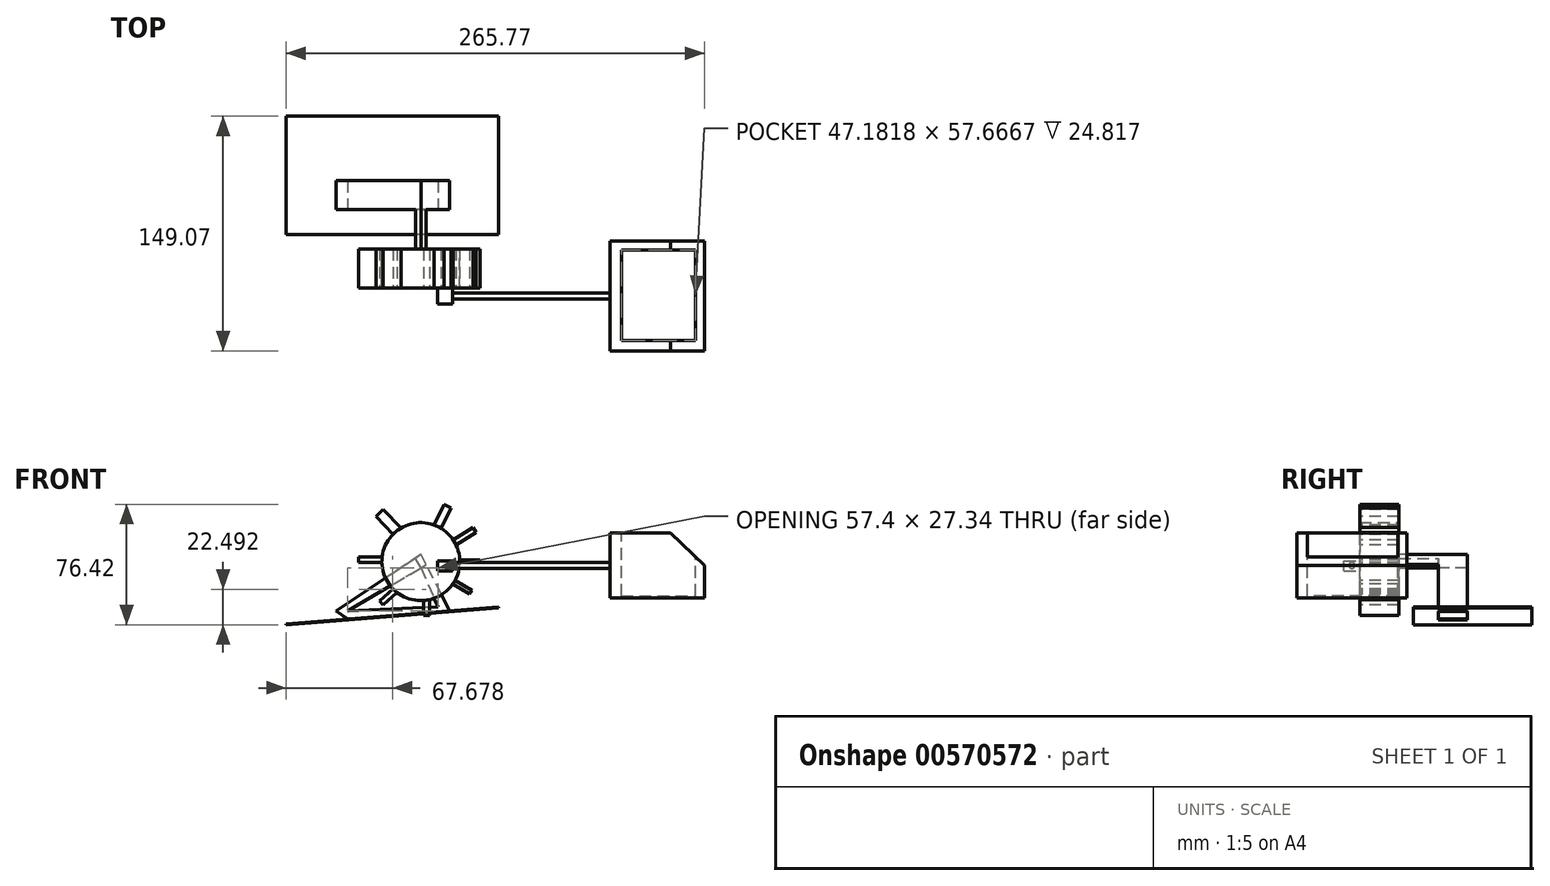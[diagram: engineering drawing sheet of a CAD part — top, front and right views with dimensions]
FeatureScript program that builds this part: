
annotation { "Feature Type Name" : "Feature", "Feature Type Description" : "" }
export const myFeature = defineFeature(function(context is Context, id is Id, definition is map)
    precondition{}
    {
        {
            var Q0;
            Q0=qCreatedBy(makeId("Top.planeOp"),FACE);
            var sketch = newSketch(context, id + "F0", { "sketchPlane" : qUnion([Q0])});
            skLineSegment(sketch, "E0.bottom", {"start": v(40, 9.15) * mm, "end": v(-40, 9.15) * mm});
            skLineSegment(sketch, "E0.top", {"start": v(40, -9.15) * mm, "end": v(-40, -9.15) * mm});
            skLineSegment(sketch, "E0.left", {"start": v(40, 9.15) * mm, "end": v(40, -9.15) * mm});
            skLineSegment(sketch, "E0.right", {"start": v(-40, 9.15) * mm, "end": v(-40, -9.15) * mm});
            skPoint(sketch, "E0.middle", {"position": v(0, 0) * mm});
            skSolve(sketch);
        }
        {
            var Q0;
            Q0=makeQuery(id+"F0.imprint","IMPRINT",FACE,{"disambiguationData":[TD([[makeQuery(id+"F0.imprint","IMPRINT",EDGE,{"derivedFrom":sQuery(id+"F0.wireOp",EDGE,"E0.bottom")}),1.0]])]});
            extrude(context, id + "F1", {"entities" : qUnion([Q0]), "depth" : 50 * mm, "offsetDistance" : 25 * mm});
        }
        {
            var Q0;
            Q0=makeQuery(id+"F1.opExtrude","SWEPT_FACE",FACE,{"disambiguationData":[OSD([sQuery(id+"F0.wireOp",EDGE,"E0.top")])]});
            var sketch = newSketch(context, id + "F2", { "sketchPlane" : qUnion([Q0])});
            skLineSegment(sketch, "E1", {"start": v(-29.15, 11.41) * mm, "end": v(17.63, 38.75) * mm});
            skLineSegment(sketch, "E2", {"start": v(17.63, 38.75) * mm, "end": v(28.25, 13.9) * mm});
            skLineSegment(sketch, "E3", {"start": v(28.25, 13.9) * mm, "end": v(-29.15, 11.41) * mm});
            skLineSegment(sketch, "E4", {"start": v(-29.15, 6.21) * mm, "end": v(35.7, 11.41) * mm});
            skLineSegment(sketch, "E5", {"start": v(35.7, 11.41) * mm, "end": v(17.63, 47.11) * mm});
            skLineSegment(sketch, "E6", {"start": v(17.63, 47.11) * mm, "end": v(-36.38, 11.41) * mm});
            skLineSegment(sketch, "E7", {"start": v(-36.38, 11.41) * mm, "end": v(-29.15, 6.21) * mm});
            skSolve(sketch);
        }
        {
            var Q0;
            Q0=makeQuery(id+"F2.imprint","IMPRINT",FACE,{"disambiguationData":[TD([[makeQuery(id+"F2.imprint","IMPRINT",EDGE,{"derivedFrom":sQuery(id+"F2.wireOp",EDGE,"E4")}),-1.0]])]});
            var Q1;
            Q1=makeQuery(id+"F2.imprint","IMPRINT",FACE,{"disambiguationData":[TD([[makeQuery(id+"F2.imprint","IMPRINT",EDGE,{"derivedFrom":sQuery(id+"F2.wireOp",EDGE,"E1")}),-1.0]])]});
            extrude(context, id + "F3", {"entities" : qUnion([Q0, Q1]), "operationType" : NewBodyOperationType.REMOVE, "endBound" : BoundingType.THROUGH_ALL, "oppositeDirection" : true, "depth" : 25 * mm, "offsetDistance" : 25 * mm});
        }
        {
            var Q0;
            Q0=makeQuery(id+"F1.opExtrude","SWEPT_FACE",FACE,{"disambiguationData":[OSD([sQuery(id+"F0.wireOp",EDGE,"E0.top")])]});
            var sketch = newSketch(context, id + "F4", { "sketchPlane" : qUnion([Q0])});
            skLineSegment(sketch, "E8", {"start": v(17.63, 38.75) * mm, "end": v(14.1, 44.78) * mm});
            skLineSegment(sketch, "E9", {"start": v(17.63, 38.75) * mm, "end": v(20.8, 40.85) * mm});
            skSolve(sketch);
        }
        {
            var Q0;
            {var subQ0=sQuery(id+"F4.wireOp",EDGE,"E8");Q0=makeQuery(id+"F4.imprint","IMPRINT",FACE,{"disambiguationData":[TD([[makeQuery(id+"F4.imprint","IMPRINT",EDGE,{"derivedFrom":subQ0}),-1.0]])]});}
            extrude(context, id + "F5", {"entities" : qUnion([Q0]), "operationType" : NewBodyOperationType.ADD, "depth" : 25 * mm, "offsetDistance" : 25 * mm});
        }
        {
            var Q0;
            Q0=makeQuery(id+"F3.boolean.opBoolean","COPY",FACE,{"derivedFrom":makeQuery(id+"F3.opExtrude","SWEPT_FACE",FACE,{"disambiguationData":[OSD([sQuery(id+"F2.wireOp",EDGE,"E4")])]})});
            var sketch = newSketch(context, id + "F6", { "sketchPlane" : qUnion([Q0])});
            skLineSegment(sketch, "E10.bottom", {"start": v(67.66, 50.07) * mm, "end": v(-67.66, 50.07) * mm});
            skLineSegment(sketch, "E10.top", {"start": v(67.66, -50.07) * mm, "end": v(-67.66, -50.07) * mm});
            skLineSegment(sketch, "E10.left", {"start": v(67.66, 50.07) * mm, "end": v(67.66, -50.07) * mm});
            skLineSegment(sketch, "E10.right", {"start": v(-67.66, 50.07) * mm, "end": v(-67.66, -50.07) * mm});
            skPoint(sketch, "E10.middle", {"position": v(0, 0) * mm});
            skSolve(sketch);
        }
        {
            var Q0;
            Q0=makeQuery(id+"F6.imprint","IMPRINT",FACE,{"disambiguationData":[TD([[makeQuery(id+"F6.imprint","IMPRINT",EDGE,{"derivedFrom":sQuery(id+"F6.wireOp",EDGE,"E10.bottom")}),1.0]])]});
            extrude(context, id + "F7", {"entities" : qUnion([Q0]), "depth" : 0.5 * mm, "offsetDistance" : 25 * mm});
        }
        {
            var Q0;
            Q0=makeQuery(id+"F5.opExtrude","CAP_FACE",FACE,{"disambiguationData":[OSD([sQuery(id+"F2.wireOp",EDGE,"E5"),sQuery(id+"F2.wireOp",EDGE,"E6"),sQuery(id+"F4.wireOp",EDGE,"E8"),sQuery(id+"F4.wireOp",EDGE,"E9")])],"isStart":false});
            var sketch = newSketch(context, id + "F8", { "sketchPlane" : qUnion([Q0])});
            skCircle(sketch, "E11", {"center": v(17.42, 42.65) * mm, "radius": 24.74 * mm});
            skLineSegment(sketch, "E12", {"start": v(42.17, 42.65) * mm, "end": v(-7.32, 42.65) * mm});
            skSolve(sketch);
        }
        {
            var Q0;
            {var subQ5=makeQuery(id+"F5.opExtrude","CAP_EDGE",EDGE,{"disambiguationData":[OSD([sQuery(id+"F4.wireOp",EDGE,"E9")])],"isStart":false});Q0=makeQuery(id+"F8.imprint","IMPRINT",FACE,{"disambiguationData":[TD([[makeQuery(id+"F8.imprint","IMPRINT",EDGE,{"derivedFrom":subQ5}),1.0]])]});}
            var Q1;
            {var subQ5=makeQuery(id+"F5.opExtrude","CAP_EDGE",EDGE,{"disambiguationData":[OSD([sQuery(id+"F2.wireOp",EDGE,"E6")])],"isStart":false});Q1=makeQuery(id+"F8.imprint","IMPRINT",FACE,{"disambiguationData":[TD([[makeQuery(id+"F8.imprint","IMPRINT",EDGE,{"derivedFrom":subQ5}),1.0]])]});}
            var Q2;
            {var subQ0=makeQuery(id+"F5.opExtrude","CAP_EDGE",EDGE,{"disambiguationData":[OSD([sQuery(id+"F2.wireOp",EDGE,"E6")])],"isStart":false});Q2=makeQuery(id+"F8.imprint","IMPRINT",FACE,{"disambiguationData":[TD([[makeQuery(id+"F8.imprint","IMPRINT",EDGE,{"derivedFrom":subQ0}),-1.0]])]});}
            var Q3;
            {var subQ0=makeQuery(id+"F5.opExtrude","CAP_EDGE",EDGE,{"disambiguationData":[OSD([sQuery(id+"F4.wireOp",EDGE,"E9")])],"isStart":false});Q3=makeQuery(id+"F8.imprint","IMPRINT",FACE,{"disambiguationData":[TD([[makeQuery(id+"F8.imprint","IMPRINT",EDGE,{"derivedFrom":subQ0}),-1.0]])]});}
            extrude(context, id + "F9", {"entities" : qUnion([Q0, Q1, Q2, Q3]), "operationType" : NewBodyOperationType.ADD, "depth" : 25 * mm, "offsetDistance" : 25 * mm});
        }
        {
            var Q0;
            Q0=makeQuery(id+"F9.opExtrude","CAP_FACE",FACE,{"disambiguationData":[OSD([sQuery(id+"F8.wireOp",EDGE,"E11")])],"isStart":false});
            var sketch = newSketch(context, id + "F10", { "sketchPlane" : qUnion([Q0])});
            skSolve(sketch);
        }
        {
            var Q0;
            Q0=makeQuery(id+"F7.opExtrude","SWEPT_FACE",FACE,{"disambiguationData":[OSD([sQuery(id+"F6.wireOp",EDGE,"E10.bottom")])]});
            extrude(context, id + "F11", {"entities" : qUnion([Q0]), "operationType" : NewBodyOperationType.REMOVE, "oppositeDirection" : true, "depth" : 25 * mm, "offsetDistance" : 25 * mm});
        }
        {
            var Q0;
            Q0=makeQuery(id+"F10.imprint","IMPRINT",FACE,{"disambiguationData":[TD([[makeQuery(id+"F10.imprint","IMPRINT",EDGE,{"derivedFrom":makeQuery(id+"F9.opExtrude","CAP_EDGE",EDGE,{"disambiguationData":[OSD([sQuery(id+"F8.wireOp",EDGE,"E11")])],"isStart":false})}),1.0]])]});
            var sketch = newSketch(context, id + "F12", { "sketchPlane" : qUnion([Q0])});
            skLineSegment(sketch, "E13", {"start": v(36.5, 43.78) * mm, "end": v(55.1, 43.78) * mm});
            skLineSegment(sketch, "E14", {"start": v(55.1, 43.78) * mm, "end": v(55.1, 41.53) * mm});
            skLineSegment(sketch, "E15", {"start": v(55.1, 41.53) * mm, "end": v(36.64, 41.53) * mm});
            skLineSegment(sketch, "E16", {"start": v(36.64, 41.53) * mm, "end": v(36.5, 43.78) * mm});
            skLineSegment(sketch, "E17", {"start": v(34.8, 33.36) * mm, "end": v(49.83, 24.52) * mm});
            skLineSegment(sketch, "E18", {"start": v(49.83, 24.52) * mm, "end": v(48.44, 22.14) * mm});
            skLineSegment(sketch, "E19", {"start": v(48.44, 22.14) * mm, "end": v(33.82, 30.73) * mm});
            skLineSegment(sketch, "E20", {"start": v(33.82, 30.73) * mm, "end": v(34.8, 33.36) * mm});
            skLineSegment(sketch, "E21", {"start": v(22.92, 25.3) * mm, "end": v(22.92, 8.55) * mm});
            skLineSegment(sketch, "E22", {"start": v(22.92, 8.55) * mm, "end": v(19.1, 8.55) * mm});
            skLineSegment(sketch, "E23", {"start": v(19.1, 8.55) * mm, "end": v(19.1, 24.91) * mm});
            skLineSegment(sketch, "E24", {"start": v(19.1, 24.91) * mm, "end": v(22.92, 25.3) * mm});
            skLineSegment(sketch, "E25", {"start": v(35.06, 54.46) * mm, "end": v(50.5, 64.23) * mm});
            skLineSegment(sketch, "E26", {"start": v(50.5, 64.23) * mm, "end": v(52.45, 61.13) * mm});
            skLineSegment(sketch, "E27", {"start": v(52.45, 61.13) * mm, "end": v(36.68, 51.16) * mm});
            skLineSegment(sketch, "E28", {"start": v(36.68, 51.16) * mm, "end": v(35.06, 54.46) * mm});
            skLineSegment(sketch, "E29", {"start": v(8.28, 32.83) * mm, "end": v(-8.74, 17.79) * mm});
            skLineSegment(sketch, "E30", {"start": v(-8.74, 17.79) * mm, "end": v(-6.47, 15.21) * mm});
            skLineSegment(sketch, "E31", {"start": v(-6.47, 15.21) * mm, "end": v(10.76, 30.43) * mm});
            skLineSegment(sketch, "E32", {"start": v(10.76, 30.43) * mm, "end": v(8.28, 32.83) * mm});
            skLineSegment(sketch, "E33", {"start": v(3.4, 42.2) * mm, "end": v(-22.07, 42.2) * mm});
            skLineSegment(sketch, "E34", {"start": v(-22.07, 42.2) * mm, "end": v(-22.07, 45.76) * mm});
            skLineSegment(sketch, "E35", {"start": v(3.26, 45.76) * mm, "end": v(3.4, 42.2) * mm});
            skLineSegment(sketch, "E36", {"start": v(3.26, 45.76) * mm, "end": v(-22.07, 45.76) * mm});
            skLineSegment(sketch, "E37", {"start": v(22.92, 59.55) * mm, "end": v(32.17, 79.01) * mm});
            skLineSegment(sketch, "E38", {"start": v(32.17, 79.01) * mm, "end": v(36.68, 76.87) * mm});
            skLineSegment(sketch, "E39", {"start": v(36.68, 76.87) * mm, "end": v(27.14, 56.81) * mm});
            skLineSegment(sketch, "E40", {"start": v(27.14, 56.81) * mm, "end": v(22.92, 59.55) * mm});
            skLineSegment(sketch, "E41", {"start": v(6.76, 52.5) * mm, "end": v(11.84, 56.63) * mm});
            skLineSegment(sketch, "E42", {"start": v(11.84, 56.63) * mm, "end": v(-6.39, 75.76) * mm});
            skLineSegment(sketch, "E43", {"start": v(-6.39, 75.76) * mm, "end": v(-11.06, 71.32) * mm});
            skLineSegment(sketch, "E44", {"start": v(-11.06, 71.32) * mm, "end": v(6.76, 52.5) * mm});
            skSolve(sketch);
        }
        {
            var Q0;
            {var subQ0=sQuery(id+"F12.wireOp",EDGE,"SsgdpK3C-5R21-uhsC-NSBb-ErE0OAdeqTcB");Q0=makeQuery(id+"F12.imprint","IMPRINT",FACE,{"disambiguationData":[TD([[makeQuery(id+"F12.imprint","IMPRINT",EDGE,{"derivedFrom":subQ0}),-1.0]])]});}
            var Q1;
            {var subQ0=sQuery(id+"F12.wireOp",EDGE,"E38");Q1=makeQuery(id+"F12.imprint","IMPRINT",FACE,{"disambiguationData":[TD([[makeQuery(id+"F12.imprint","IMPRINT",EDGE,{"derivedFrom":subQ0}),-1.0]])]});}
            var Q2;
            {var subQ0=sQuery(id+"F12.wireOp",EDGE,"E26");Q2=makeQuery(id+"F12.imprint","IMPRINT",FACE,{"disambiguationData":[TD([[makeQuery(id+"F12.imprint","IMPRINT",EDGE,{"derivedFrom":subQ0}),-1.0]])]});}
            var Q3;
            {var subQ0=sQuery(id+"F12.wireOp",EDGE,"E18");Q3=makeQuery(id+"F12.imprint","IMPRINT",FACE,{"disambiguationData":[TD([[makeQuery(id+"F12.imprint","IMPRINT",EDGE,{"derivedFrom":subQ0}),-1.0]])]});}
            var Q4;
            {var subQ0=sQuery(id+"F12.wireOp",EDGE,"E34");Q4=makeQuery(id+"F12.imprint","IMPRINT",FACE,{"disambiguationData":[TD([[makeQuery(id+"F12.imprint","IMPRINT",EDGE,{"derivedFrom":subQ0}),-1.0]])]});}
            var Q5;
            {var subQ0=sQuery(id+"F12.wireOp",EDGE,"E14");Q5=makeQuery(id+"F12.imprint","IMPRINT",FACE,{"disambiguationData":[TD([[makeQuery(id+"F12.imprint","IMPRINT",EDGE,{"derivedFrom":subQ0}),-1.0]])]});}
            var Q6;
            {var subQ0=sQuery(id+"F12.wireOp",EDGE,"E22");Q6=makeQuery(id+"F12.imprint","IMPRINT",FACE,{"disambiguationData":[TD([[makeQuery(id+"F12.imprint","IMPRINT",EDGE,{"derivedFrom":subQ0}),-1.0]])]});}
            var Q7;
            {var subQ0=sQuery(id+"F12.wireOp",EDGE,"E30");Q7=makeQuery(id+"F12.imprint","IMPRINT",FACE,{"disambiguationData":[TD([[makeQuery(id+"F12.imprint","IMPRINT",EDGE,{"derivedFrom":subQ0}),1.0]])]});}
            var Q8;
            {var subQ0=sQuery(id+"F12.wireOp",EDGE,"E43");Q8=makeQuery(id+"F12.imprint","IMPRINT",FACE,{"disambiguationData":[TD([[makeQuery(id+"F12.imprint","IMPRINT",EDGE,{"derivedFrom":subQ0}),1.0]])]});}
            extrude(context, id + "F13", {"entities" : qUnion([Q0, Q1, Q2, Q3, Q4, Q5, Q6, Q7, Q8]), "oppositeDirection" : true, "depth" : 25 * mm, "offsetDistance" : 25 * mm});
        }
        {
            var Q0;
            Q0=makeQuery(id+"F10.imprint","IMPRINT",FACE,{"disambiguationData":[TD([[makeQuery(id+"F10.imprint","IMPRINT",EDGE,{"derivedFrom":makeQuery(id+"F9.opExtrude","CAP_EDGE",EDGE,{"disambiguationData":[OSD([sQuery(id+"F8.wireOp",EDGE,"E11")])],"isStart":false})}),1.0]])]});
            var sketch = newSketch(context, id + "F14", { "sketchPlane" : qUnion([Q0])});
            skLineSegment(sketch, "E45.bottom", {"start": v(37.64, 36.7) * mm, "end": v(28.2, 36.7) * mm});
            skLineSegment(sketch, "E45.top", {"start": v(37.64, 43) * mm, "end": v(28.2, 43) * mm});
            skLineSegment(sketch, "E45.left", {"start": v(37.64, 36.7) * mm, "end": v(37.64, 43) * mm});
            skLineSegment(sketch, "E45.right", {"start": v(28.2, 36.7) * mm, "end": v(28.2, 43) * mm});
            skSolve(sketch);
        }
        {
            var Q0;
            Q0=makeQuery(id+"F14.imprint","IMPRINT",FACE,{"disambiguationData":[TD([[makeQuery(id+"F14.imprint","IMPRINT",EDGE,{"derivedFrom":sQuery(id+"F14.wireOp",EDGE,"E45.bottom")}),-1.0]])]});
            extrude(context, id + "F15", {"entities" : qUnion([Q0]), "operationType" : NewBodyOperationType.ADD, "depth" : 10 * mm, "offsetDistance" : 25 * mm});
        }
        {
            var Q0;
            Q0=makeQuery(id+"F15.opExtrude","SWEPT_FACE",FACE,{"disambiguationData":[OSD([sQuery(id+"F14.wireOp",EDGE,"E45.left")])]});
            var sketch = newSketch(context, id + "F16", { "sketchPlane" : qUnion([Q0])});
            skCircle(sketch, "E46", {"center": v(-64.15, 40.28) * mm, "radius": 1.9 * mm});
            skPoint(sketch, "E46.centerSnap0", {"position": v(-64.15, 43) * mm});
            skSolve(sketch);
        }
        {
            var Q0;
            Q0=makeQuery(id+"F16.imprint","IMPRINT",FACE,{"disambiguationData":[TD([[makeQuery(id+"F16.imprint","IMPRINT",EDGE,{"derivedFrom":sQuery(id+"F16.wireOp",EDGE,"E46")}),1.0]])]});
            extrude(context, id + "F17", {"entities" : qUnion([Q0]), "operationType" : NewBodyOperationType.ADD, "depth" : 100 * mm, "offsetDistance" : 25 * mm});
        }
        {
            var Q0;
            Q0=makeQuery(id+"F17.opExtrude","CAP_FACE",FACE,{"disambiguationData":[OSD([sQuery(id+"F16.wireOp",EDGE,"E46")])],"isStart":false});
            var sketch = newSketch(context, id + "F18", { "sketchPlane" : qUnion([Q0])});
            skLineSegment(sketch, "E47.bottom", {"start": v(-29.3, 60.85) * mm, "end": v(-99, 60.85) * mm});
            skLineSegment(sketch, "E47.top", {"start": v(-29.3, 19.7) * mm, "end": v(-99, 19.7) * mm});
            skLineSegment(sketch, "E47.left", {"start": v(-29.3, 60.85) * mm, "end": v(-29.3, 19.7) * mm});
            skLineSegment(sketch, "E47.right", {"start": v(-99, 60.85) * mm, "end": v(-99, 19.7) * mm});
            skPoint(sketch, "E47.middle", {"position": v(-64.15, 40.28) * mm});
            skSolve(sketch);
        }
        {
            var Q0;
            Q0=makeQuery(id+"F18.imprint","IMPRINT",FACE,{"disambiguationData":[TD([[makeQuery(id+"F18.imprint","IMPRINT",EDGE,{"derivedFrom":makeQuery(id+"F17.opExtrude","CAP_EDGE",EDGE,{"disambiguationData":[OSD([sQuery(id+"F16.wireOp",EDGE,"E46")])],"isStart":false})}),1.0]])]});
            var Q1;
            Q1=makeQuery(id+"F18.imprint","IMPRINT",FACE,{"disambiguationData":[TD([[makeQuery(id+"F18.imprint","IMPRINT",EDGE,{"derivedFrom":sQuery(id+"F18.wireOp",EDGE,"E47.bottom")}),1.0]])]});
            extrude(context, id + "F19", {"entities" : qUnion([Q0, Q1]), "depth" : 60 * mm, "offsetDistance" : 25 * mm});
        }
        {
            var Q0;
            Q0=makeQuery(id+"F19.opExtrude","SWEPT_FACE",FACE,{"disambiguationData":[OSD([sQuery(id+"F18.wireOp",EDGE,"E47.bottom")])]});
            var sketch = newSketch(context, id + "F20", { "sketchPlane" : qUnion([Q0])});
            skLineSegment(sketch, "E48.bottom", {"start": v(144.8, -34.8) * mm, "end": v(191.99, -34.8) * mm});
            skLineSegment(sketch, "E48.top", {"start": v(144.8, -92.47) * mm, "end": v(191.99, -92.47) * mm});
            skLineSegment(sketch, "E48.left", {"start": v(144.8, -34.8) * mm, "end": v(144.8, -92.47) * mm});
            skLineSegment(sketch, "E48.right", {"start": v(191.99, -34.8) * mm, "end": v(191.99, -92.47) * mm});
            skPoint(sketch, "E48.middle", {"position": v(168.4, -63.64) * mm});
            skSolve(sketch);
        }
        {
            var Q0;
            Q0=makeQuery(id+"F20.imprint","IMPRINT",FACE,{"disambiguationData":[TD([[makeQuery(id+"F20.imprint","IMPRINT",EDGE,{"derivedFrom":sQuery(id+"F20.wireOp",EDGE,"E48.bottom")}),-1.0]])]});
            extrude(context, id + "F21", {"entities" : qUnion([Q0]), "operationType" : NewBodyOperationType.REMOVE, "oppositeDirection" : true, "depth" : 40 * mm, "offsetDistance" : 25 * mm});
        }
        {
            var Q0;
            Q0=makeQuery(id+"F19.opExtrude","SWEPT_FACE",FACE,{"disambiguationData":[OSD([sQuery(id+"F18.wireOp",EDGE,"E47.right")])]});
            var sketch = newSketch(context, id + "F22", { "sketchPlane" : qUnion([Q0])});
            skLineSegment(sketch, "E49", {"start": v(176.06, 60.85) * mm, "end": v(197.64, 40.28) * mm});
            skSolve(sketch);
        }
        {
            var Q0;
            {var subQ0=sQuery(id+"F22.wireOp",EDGE,"E49");Q0=makeQuery(id+"F22.imprint","IMPRINT",FACE,{"disambiguationData":[TD([[makeQuery(id+"F22.imprint","IMPRINT",EDGE,{"derivedFrom":subQ0}),1.0]])]});}
            extrude(context, id + "F23", {"entities" : qUnion([Q0]), "operationType" : NewBodyOperationType.REMOVE, "endBound" : BoundingType.THROUGH_ALL, "oppositeDirection" : true, "depth" : 25 * mm, "offsetDistance" : 25 * mm});
        }
    });
